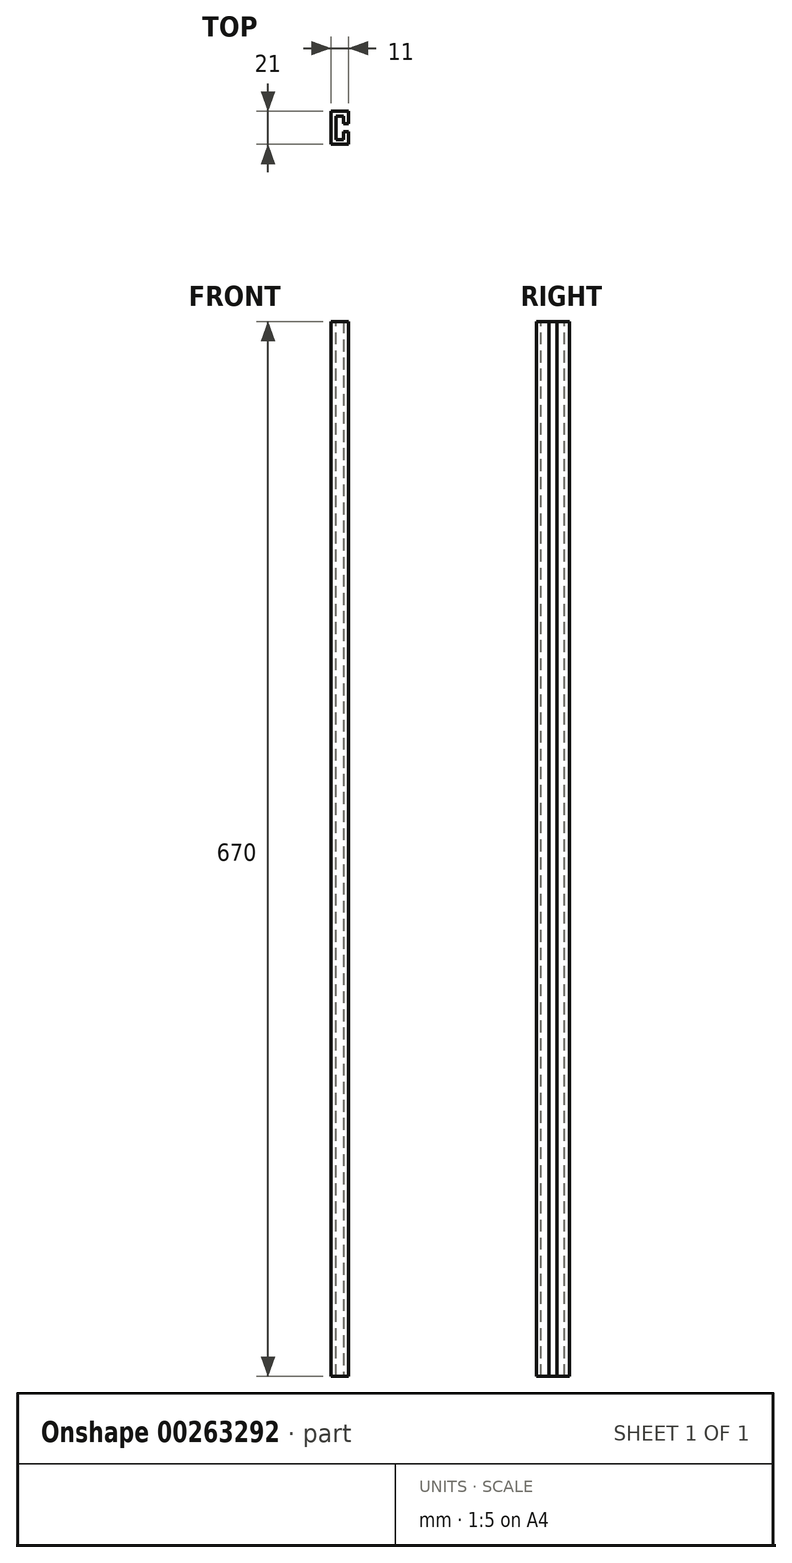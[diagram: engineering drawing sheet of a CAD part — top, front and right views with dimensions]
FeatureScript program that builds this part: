
annotation { "Feature Type Name" : "Feature", "Feature Type Description" : "" }
export const myFeature = defineFeature(function(context is Context, id is Id, definition is map)
    precondition{}
    {
        {
            var Q0;
            Q0=qCreatedBy(makeId("Top.planeOp"),FACE);
            var sketch = newSketch(context, id + "F0", { "sketchPlane" : qUnion([Q0])});
            skLineSegment(sketch, "E0.bottom", {"start": v(5.5, -10.5) * mm, "end": v(-5.5, -10.5) * mm});
            skLineSegment(sketch, "E0.top", {"start": v(5.5, 10.5) * mm, "end": v(-5.5, 10.5) * mm});
            skLineSegment(sketch, "E0.left", {"start": v(5.5, -10.5) * mm, "end": v(5.5, 10.5) * mm});
            skLineSegment(sketch, "E0.right", {"start": v(-5.5, -10.5) * mm, "end": v(-5.5, 10.5) * mm});
            skPoint(sketch, "E0.middle", {"position": v(0, 0) * mm});
            skSolve(sketch);
        }
        {
            var Q0;
            Q0 = qSketchRegion(id + "F0", true);
            extrude(context, id + "F1", {"entities" : qUnion([Q0]), "depth" : 670 * mm});
        }
        {
            var Q0;
            Q0=makeQuery(id+"F1.opExtrude","CAP_FACE",FACE,{"disambiguationData":[OSD([sQuery(id+"F0.wireOp",EDGE,"E0.bottom"),sQuery(id+"F0.wireOp",EDGE,"E0.top"),sQuery(id+"F0.wireOp",EDGE,"E0.left"),sQuery(id+"F0.wireOp",EDGE,"E0.right")])],"isStart":false});
            var sketch = newSketch(context, id + "F2", { "sketchPlane" : qUnion([Q0])});
            skLineSegment(sketch, "E1.bottom", {"start": v(2.5, -7.5) * mm, "end": v(-2.5, -7.5) * mm});
            skLineSegment(sketch, "E1.top", {"start": v(2.5, 7.5) * mm, "end": v(-2.5, 7.5) * mm});
            skLineSegment(sketch, "E1.left", {"start": v(2.5, -7.5) * mm, "end": v(2.5, 7.5) * mm});
            skLineSegment(sketch, "E1.right", {"start": v(-2.5, -7.5) * mm, "end": v(-2.5, 7.5) * mm});
            skPoint(sketch, "E1.middle", {"position": v(0, 0) * mm});
            skSolve(sketch);
        }
        {
            var Q0;
            Q0 = qSketchRegion(id + "F2", true);
            extrude(context, id + "F3", {"entities" : qUnion([Q0]), "operationType" : NewBodyOperationType.REMOVE, "oppositeDirection" : true, "depth" : 670 * mm});
        }
        {
            var Q0;
            Q0=makeQuery(id+"F1.opExtrude","CAP_FACE",FACE,{"disambiguationData":[OSD([sQuery(id+"F0.wireOp",EDGE,"E0.bottom"),sQuery(id+"F0.wireOp",EDGE,"E0.top"),sQuery(id+"F0.wireOp",EDGE,"E0.left"),sQuery(id+"F0.wireOp",EDGE,"E0.right")])],"isStart":false});
            var sketch = newSketch(context, id + "F4", { "sketchPlane" : qUnion([Q0])});
            skLineSegment(sketch, "E2.bottom", {"start": v(0, 0) * mm, "end": v(10.77, 0) * mm});
            skLineSegment(sketch, "E2.top", {"start": v(0, -2.4) * mm, "end": v(10.77, -2.4) * mm});
            skLineSegment(sketch, "E2.left", {"start": v(0, 0) * mm, "end": v(0, -2.4) * mm});
            skLineSegment(sketch, "E2.right", {"start": v(10.77, 0) * mm, "end": v(10.77, -2.4) * mm});
            skPoint(sketch, "E3.oppositeSnap0", {"position": v(10.77, -1.2) * mm});
            skLineSegment(sketch, "E3.top", {"start": v(0, 2.6) * mm, "end": v(10.77, 2.6) * mm});
            skLineSegment(sketch, "E3.left", {"start": v(0, 0) * mm, "end": v(0, 2.6) * mm});
            skLineSegment(sketch, "E3.right", {"start": v(10.77, 0) * mm, "end": v(10.77, 2.6) * mm});
            skSolve(sketch);
        }
        {
            var Q0;
            Q0 = qSketchRegion(id + "F4", true);
            extrude(context, id + "F5", {"entities" : qUnion([Q0]), "operationType" : NewBodyOperationType.REMOVE, "oppositeDirection" : true, "depth" : 670 * mm});
        }
    });
